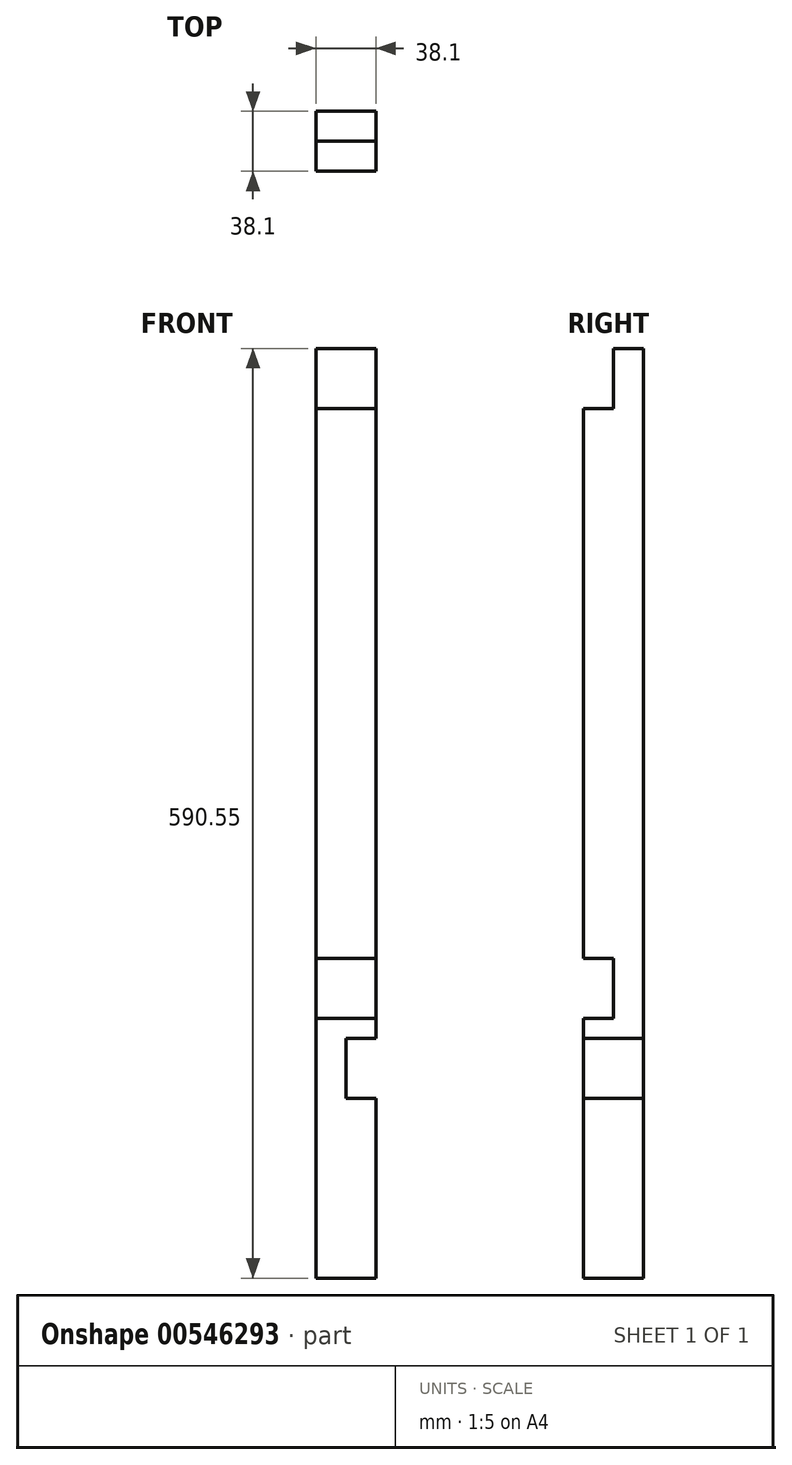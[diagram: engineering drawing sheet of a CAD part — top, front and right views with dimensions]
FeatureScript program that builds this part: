
annotation { "Feature Type Name" : "Feature", "Feature Type Description" : "" }
export const myFeature = defineFeature(function(context is Context, id is Id, definition is map)
    precondition{}
    {
        {
            var Q0;
            Q0=qCreatedBy(makeId("Top.planeOp"),FACE);
            var sketch = newSketch(context, id + "F0", { "sketchPlane" : qUnion([Q0])});
            skLineSegment(sketch, "E0", {"start": v(-53.07, 41.71) * mm, "end": v(-14.97, 41.71) * mm});
            skLineSegment(sketch, "E1", {"start": v(-14.97, 41.71) * mm, "end": v(-14.97, 3.61) * mm});
            skLineSegment(sketch, "E2", {"start": v(-14.97, 3.61) * mm, "end": v(-53.07, 3.61) * mm});
            skLineSegment(sketch, "E3", {"start": v(-53.07, 3.61) * mm, "end": v(-53.07, 41.71) * mm});
            skSolve(sketch);
        }
        {
            var Q0;
            Q0=makeQuery(id+"F0.imprint","IMPRINT",FACE,{"disambiguationData":[TD([[makeQuery(id+"F0.imprint","IMPRINT",EDGE,{"derivedFrom":sQuery(id+"F0.wireOp",EDGE,"E0")}),-1.0]])]});
            extrude(context, id + "F1", {"entities" : qUnion([Q0]), "depth" : 590.55 * mm, "offsetDistance" : 25.4 * mm});
        }
        {
            var Q0;
            Q0=makeQuery(id+"F1.opExtrude","SWEPT_FACE",FACE,{"disambiguationData":[OSD([sQuery(id+"F0.wireOp",EDGE,"E2")])]});
            var sketch = newSketch(context, id + "F2", { "sketchPlane" : qUnion([Q0])});
            skLineSegment(sketch, "E4", {"start": v(-53.07, 590.55) * mm, "end": v(-53.07, 552.45) * mm});
            skLineSegment(sketch, "E5", {"start": v(-53.07, 552.45) * mm, "end": v(-14.97, 552.45) * mm});
            skLineSegment(sketch, "E6", {"start": v(-14.97, 552.45) * mm, "end": v(-14.97, 590.55) * mm});
            skLineSegment(sketch, "E7", {"start": v(-14.97, 590.55) * mm, "end": v(-53.07, 590.55) * mm});
            skSolve(sketch);
        }
        {
            var Q0;
            Q0 = qSketchRegion(id + "F2", true);
            extrude(context, id + "F3", {"entities" : qUnion([Q0]), "operationType" : NewBodyOperationType.REMOVE, "oppositeDirection" : true, "depth" : 19.05 * mm, "offsetDistance" : 25.4 * mm});
        }
        {
            var Q0;
            Q0=makeQuery(id+"F1.opExtrude","SWEPT_FACE",FACE,{"disambiguationData":[OSD([sQuery(id+"F0.wireOp",EDGE,"E1")])]});
            var sketch = newSketch(context, id + "F4", { "sketchPlane" : qUnion([Q0])});
            skLineSegment(sketch, "E8", {"start": v(41.71, 0) * mm, "end": v(41.71, 152.4) * mm});
            skLineSegment(sketch, "E9", {"start": v(41.71, 152.4) * mm, "end": v(3.61, 152.4) * mm});
            skLineSegment(sketch, "E10", {"start": v(3.61, 152.4) * mm, "end": v(3.61, 114.3) * mm});
            skLineSegment(sketch, "E11", {"start": v(3.61, 114.3) * mm, "end": v(41.71, 114.3) * mm});
            skLineSegment(sketch, "E12", {"start": v(41.71, 114.3) * mm, "end": v(41.71, 152.4) * mm});
            skSolve(sketch);
        }
        {
            var Q0;
            Q0 = qSketchRegion(id + "F4", true);
            extrude(context, id + "F5", {"entities" : qUnion([Q0]), "operationType" : NewBodyOperationType.REMOVE, "oppositeDirection" : true, "depth" : 19.05 * mm, "offsetDistance" : 25.4 * mm});
        }
        {
            var Q0;
            Q0=makeQuery(id+"F1.opExtrude","SWEPT_FACE",FACE,{"disambiguationData":[OSD([sQuery(id+"F0.wireOp",EDGE,"E2")])]});
            var sketch = newSketch(context, id + "F6", { "sketchPlane" : qUnion([Q0])});
            skLineSegment(sketch, "E13", {"start": v(-53.07, 0) * mm, "end": v(-53.07, 203.2) * mm});
            skLineSegment(sketch, "E14", {"start": v(-53.07, 203.2) * mm, "end": v(-14.97, 203.2) * mm});
            skLineSegment(sketch, "E15", {"start": v(-14.97, 203.2) * mm, "end": v(-14.97, 165.1) * mm});
            skLineSegment(sketch, "E16", {"start": v(-14.97, 165.1) * mm, "end": v(-53.07, 165.1) * mm});
            skLineSegment(sketch, "E17", {"start": v(-53.07, 165.1) * mm, "end": v(-53.07, 203.2) * mm});
            skSolve(sketch);
        }
        {
            var Q0;
            Q0 = qSketchRegion(id + "F6", true);
            extrude(context, id + "F7", {"entities" : qUnion([Q0]), "operationType" : NewBodyOperationType.REMOVE, "oppositeDirection" : true, "depth" : 19.05 * mm, "offsetDistance" : 25.4 * mm});
        }
    });
